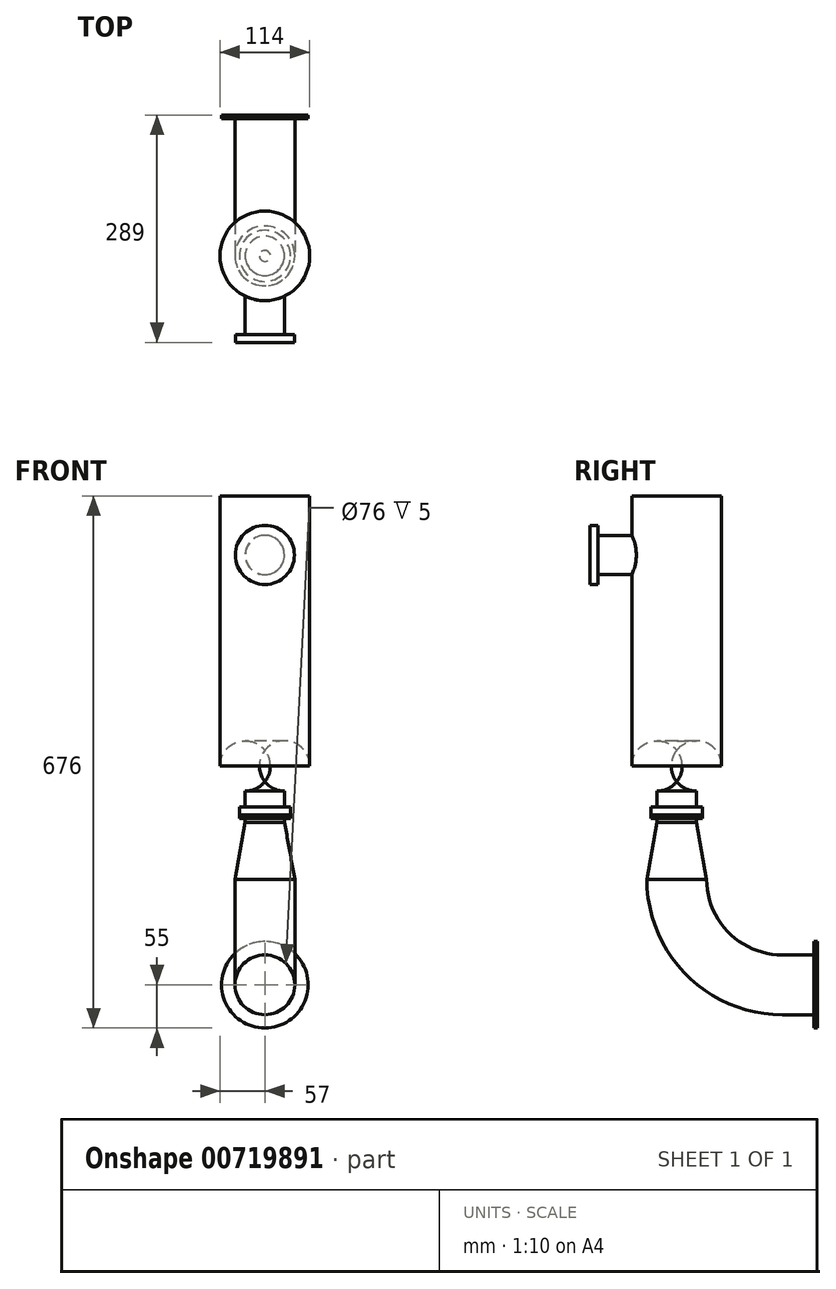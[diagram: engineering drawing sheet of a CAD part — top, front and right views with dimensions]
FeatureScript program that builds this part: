
annotation { "Feature Type Name" : "Feature", "Feature Type Description" : "" }
export const myFeature = defineFeature(function(context is Context, id is Id, definition is map)
    precondition{}
    {
        {
            var Q0;
            Q0=qCreatedBy(makeId("Top.planeOp"),FACE);
            var sketch = newSketch(context, id + "F0", { "sketchPlane" : qUnion([Q0])});
            skCircle(sketch, "E0", {"center": v(0, 0) * mm, "radius": 57 * mm});
            skSolve(sketch);
        }
        {
            var Q0;
            Q0=makeQuery(id+"F0.imprint","IMPRINT",FACE,{"disambiguationData":[TD([[makeQuery(id+"F0.imprint","IMPRINT",EDGE,{"derivedFrom":sQuery(id+"F0.wireOp",EDGE,"E0")}),1.0]])]});
            extrude(context, id + "F1", {"entities" : qUnion([Q0]), "depth" : 375 * mm, "offsetDistance" : 25 * mm});
        }
        {
            var Q0;
            Q0=makeQuery(id+"F1.opExtrude","CAP_EDGE",EDGE,{"disambiguationData":[OSD([sQuery(id+"F0.wireOp",EDGE,"E0")])],"isStart":true});
            fillet(context, id + "F2", {"entities" : qUnion([Q0]), "radius" : 32 * mm, "tangentPropagation" : true, "allowEdgeOverflow" : false});
        }
        {
            var Q0;
            Q0=qCreatedBy(makeId("Front.planeOp"),FACE);
            var sketch = newSketch(context, id + "F3", { "sketchPlane" : qUnion([Q0])});
            skCircle(sketch, "E1", {"center": v(0, 300) * mm, "radius": 25 * mm});
            skSolve(sketch);
        }
        {
            var Q0;
            Q0 = qSketchRegion(id + "F3", true);
            extrude(context, id + "F4", {"entities" : qUnion([Q0]), "operationType" : NewBodyOperationType.ADD, "depth" : 110 * mm, "offsetDistance" : 25 * mm});
        }
        {
            var Q0;
            Q0=makeQuery(id+"F4.opExtrude","CAP_FACE",FACE,{"disambiguationData":[OSD([sQuery(id+"F3.wireOp",EDGE,"E1")])],"isStart":false});
            var sketch = newSketch(context, id + "F5", { "sketchPlane" : qUnion([Q0])});
            skCircle(sketch, "E2", {"center": v(0, 300) * mm, "radius": 37.5 * mm});
            skSolve(sketch);
        }
        {
            var Q0;
            Q0=makeQuery(id+"F5.imprint","IMPRINT",FACE,{"disambiguationData":[TD([[makeQuery(id+"F5.imprint","IMPRINT",EDGE,{"derivedFrom":sQuery(id+"F5.wireOp",EDGE,"E2")}),1.0]])]});
            extrude(context, id + "F6", {"entities" : qUnion([Q0]), "operationType" : NewBodyOperationType.ADD, "oppositeDirection" : true, "depth" : 10 * mm, "offsetDistance" : 25 * mm});
        }
        {
            var Q0;
            Q0=makeQuery(id+"F1.opExtrude","CAP_FACE",FACE,{"disambiguationData":[OSD([sQuery(id+"F0.wireOp",EDGE,"E0")])],"isStart":true});
            var sketch = newSketch(context, id + "F7", { "sketchPlane" : qUnion([Q0])});
            skCircle(sketch, "E3", {"center": v(0, 0) * mm, "radius": 25 * mm});
            skSolve(sketch);
        }
        {
            var Q0;
            Q0=makeQuery(id+"F7.imprint","IMPRINT",FACE,{"disambiguationData":[TD([[makeQuery(id+"F7.imprint","IMPRINT",EDGE,{"derivedFrom":sQuery(id+"F7.wireOp",EDGE,"E3")}),1.0]])]});
            extrude(context, id + "F8", {"entities" : qUnion([Q0]), "operationType" : NewBodyOperationType.ADD, "depth" : 30 * mm, "offsetDistance" : 25 * mm});
        }
        {
            var Q0;
            Q0=makeQuery(id+"F8.opExtrude","CAP_FACE",FACE,{"disambiguationData":[OSD([sQuery(id+"F7.wireOp",EDGE,"E3")])],"isStart":false});
            var sketch = newSketch(context, id + "F9", { "sketchPlane" : qUnion([Q0])});
            skCircle(sketch, "E4", {"center": v(0, 0) * mm, "radius": 32.5 * mm});
            skSolve(sketch);
        }
        {
            var Q0;
            Q0=makeQuery(id+"F9.imprint","IMPRINT",FACE,{"disambiguationData":[TD([[makeQuery(id+"F9.imprint","IMPRINT",EDGE,{"derivedFrom":sQuery(id+"F9.wireOp",EDGE,"E4")}),1.0]])]});
            extrude(context, id + "F10", {"entities" : qUnion([Q0]), "operationType" : NewBodyOperationType.ADD, "oppositeDirection" : true, "depth" : 10 * mm, "offsetDistance" : 25 * mm});
        }
        {
            var Q0;
            {var subQ0=sQuery(id+"F7.wireOp",EDGE,"E3");Q0=makeQuery(id+"F10.boolean.opBoolean","MERGE",FACE,{"derivedFrom":[makeQuery(id+"F8.opExtrude","CAP_FACE",FACE,{"disambiguationData":[OSD([subQ0])],"isStart":false}),makeQuery(id+"F10.opExtrude","CAP_FACE",FACE,{"disambiguationData":[OSD([subQ0,sQuery(id+"F9.wireOp",EDGE,"E4")])],"isStart":true})]});}
            cPlane(context, id + "F11", {"entities" : qUnion([Q0]), "cplaneType" : CPlaneType.OFFSET, "offset" : 1 * mm, "width" : 150 * mm, "height" : 150 * mm});
        }
        {
            var Q0;
            Q0=qCreatedBy(id+"F11.planeOp",FACE);
            var sketch = newSketch(context, id + "F12", { "sketchPlane" : qUnion([Q0])});
            skCircle(sketch, "E5", {"center": v(0, 0) * mm, "radius": 25 * mm});
            skSolve(sketch);
        }
        {
            var Q0;
            Q0=makeQuery(id+"F12.imprint","IMPRINT",FACE,{"disambiguationData":[TD([[makeQuery(id+"F12.imprint","IMPRINT",EDGE,{"derivedFrom":sQuery(id+"F12.wireOp",EDGE,"E5")}),1.0]])]});
            extrude(context, id + "F13", {"entities" : qUnion([Q0]), "depth" : 9 * mm, "offsetDistance" : 25 * mm});
        }
        {
            var Q0;
            Q0=makeQuery(id+"F13.opExtrude","CAP_FACE",FACE,{"disambiguationData":[OSD([sQuery(id+"F12.wireOp",EDGE,"E5")])],"isStart":true});
            var sketch = newSketch(context, id + "F14", { "sketchPlane" : qUnion([Q0])});
            skCircle(sketch, "E6", {"center": v(0, 0) * mm, "radius": 32.5 * mm});
            skSolve(sketch);
        }
        {
            var Q0;
            Q0=makeQuery(id+"F14.imprint","IMPRINT",FACE,{"disambiguationData":[TD([[makeQuery(id+"F14.imprint","IMPRINT",EDGE,{"derivedFrom":sQuery(id+"F14.wireOp",EDGE,"E6")}),1.0]])]});
            extrude(context, id + "F15", {"entities" : qUnion([Q0]), "operationType" : NewBodyOperationType.ADD, "oppositeDirection" : true, "depth" : 4 * mm, "offsetDistance" : 25 * mm});
        }
        {
            var Q0;
            Q0=qCreatedBy(makeId("Front.planeOp"),FACE);
            var sketch = newSketch(context, id + "F16", { "sketchPlane" : qUnion([Q0])});
            skLineSegment(sketch, "E7.0", {"start": v(25, -40) * mm, "end": v(-25, -40) * mm});
            skLineSegment(sketch, "E8", {"start": v(0, -40) * mm, "end": v(0, -112) * mm});
            skLineSegment(sketch, "E9", {"start": v(-25, -40) * mm, "end": v(-38, -112) * mm});
            skLineSegment(sketch, "E10", {"start": v(0, -112) * mm, "end": v(-38, -112) * mm});
            skSolve(sketch);
        }
        {
            var Q0;
            {var subQ2=sQuery(id+"F16.wireOp",EDGE,"E8");Q0=makeQuery(id+"F16.imprint","IMPRINT",FACE,{"disambiguationData":[TD([[makeQuery(id+"F16.imprint","IMPRINT",EDGE,{"derivedFrom":subQ2}),-1.0]])]});}
            var Q1;
            Q1=sQuery(id+"F16.wireOp",EDGE,"E8");
            revolve(context, id + "F17", {"operationType" : NewBodyOperationType.ADD, "surfaceOperationType" : NewSurfaceOperationType.NEW, "entities" : qUnion([Q0]), "axis" : qUnion([Q1]), "revolveType" : RevolveType.FULL});
        }
        {
            var Q0;
            Q0=makeQuery(id+"F17.opRevolve","SWEPT_FACE",FACE,{"disambiguationData":[OSD([sQuery(id+"F16.wireOp",EDGE,"E10")])]});
            var sketch = newSketch(context, id + "F18", { "sketchPlane" : qUnion([Q0])});
            skCircle(sketch, "E11.0", {"center": v(0, 0) * mm, "radius": 38 * mm});
            skLineSegment(sketch, "E12", {"start": v(0, 0) * mm, "end": v(0, -134) * mm, "construction": true});
            skLineSegment(sketch, "E13", {"start": v(0, -134) * mm, "end": v(-30.46, -134) * mm, "construction": true});
            skSolve(sketch);
        }
        {
            var Q0;
            Q0=makeQuery(id+"F18.imprint","IMPRINT",FACE,{"disambiguationData":[TD([[makeQuery(id+"F18.imprint","IMPRINT",EDGE,{"derivedFrom":sQuery(id+"F18.wireOp",EDGE,"E11.0")}),-1.0]])]});
            var Q1;
            Q1=sQuery(id+"F18.wireOp",EDGE,"E13");
            revolve(context, id + "F19", {"surfaceOperationType" : NewSurfaceOperationType.NEW, "entities" : qUnion([Q0]), "axis" : qUnion([Q1]), "revolveType" : RevolveType.ONE_DIRECTION, "oppositeDirection" : true, "angle" : 90 * degree});
        }
        {
            var Q0;
            Q0=makeQuery(id+"F19.opRevolve","CAP_FACE",FACE,{"disambiguationData":[OSD([sQuery(id+"F18.wireOp",EDGE,"E11.0")])],"isStart":false});
            var sketch = newSketch(context, id + "F20", { "sketchPlane" : qUnion([Q0])});
            skCircle(sketch, "E14.0", {"center": v(0, -246) * mm, "radius": 38 * mm});
            skSolve(sketch);
        }
        {
            var Q0;
            Q0=makeQuery(id+"F20.imprint","IMPRINT",FACE,{"disambiguationData":[TD([[makeQuery(id+"F20.imprint","IMPRINT",EDGE,{"derivedFrom":sQuery(id+"F20.wireOp",EDGE,"E14.0")}),-1.0]])]});
            extrude(context, id + "F21", {"entities" : qUnion([Q0]), "operationType" : NewBodyOperationType.ADD, "depth" : 45 * mm, "offsetDistance" : 25 * mm});
        }
        {
            var Q0;
            Q0=makeQuery(id+"F21.opExtrude","CAP_FACE",FACE,{"disambiguationData":[OSD([sQuery(id+"F20.wireOp",EDGE,"E14.0")])],"isStart":false});
            var sketch = newSketch(context, id + "F22", { "sketchPlane" : qUnion([Q0])});
            skCircle(sketch, "E15", {"center": v(0, -246) * mm, "radius": 55 * mm});
            skSolve(sketch);
        }
        {
            var Q0;
            Q0=makeQuery(id+"F22.imprint","IMPRINT",FACE,{"disambiguationData":[TD([[makeQuery(id+"F22.imprint","IMPRINT",EDGE,{"derivedFrom":sQuery(id+"F22.wireOp",EDGE,"E15")}),1.0]])]});
            extrude(context, id + "F23", {"entities" : qUnion([Q0]), "oppositeDirection" : true, "depth" : 5 * mm, "offsetDistance" : 25 * mm});
        }
    });
